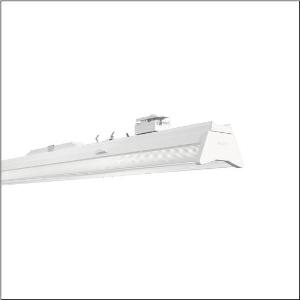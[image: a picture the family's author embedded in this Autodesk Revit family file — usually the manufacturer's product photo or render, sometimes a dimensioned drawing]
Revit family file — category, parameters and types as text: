
# Revit family: licross_r__21_performance_mo_52td16dn4a5g_459a
name_source: partatom
category: Lighting Fixtures
units: mm (PartAtom-declared; Revit-internal decimal feet)

## family parameters
Cut with Voids When Loaded = No
Host = Face
Light Source = No
Part Type = Normal
Room Calculation Point = No
Round Connector Dimension = Use Diameter
Shared = No

## types (1)
- --- (1 x LED, 10840 lm, 62 W, 4000K)
    Apparent Load = 62 VA
    CIE Flux Codes = 66 88 96 79 100
    Color Rendering = 80
    Color Temperature = 4000K
    Default Elevation = 1800 mm
    Description = Licross® 21 Performance MO, luminaire insert, of sheet steel, galvanised, coil coated, white, length: 1.500mm, width: 120mm, height: 123mm, LED rated luminous flux: 10.840lm, light colour: 840, control gear: DALI 2, with plug, 5-pole, with phase selection, mains connection: 220..240V, AC, 50/60Hz, rated input power: 62W, halogen-free wiring, primary light control with lens, of plastic, primary optical cover: cover, of PMMA, light emission: direct/indirect distribution, primary light characteristic: symmetric, protection rating (complete): IP54, insulation class (complete): insulation class I (protective earthing), certification: CE, ENEC, VDE, UKCA, protection symbol: D if used in an environment with non-conductive dust loads with corresponding accessories, impact resistance: IK06, permissible ambient temperature for indoor applications: -25..+35°C, corresponds to IFS (International Featured Standards) requirements for safety and quality in the food industry, reducing of maximum allowable ambient temperature of 5°C with ceiling mounting, LABS conformity tested according to VDMA 24364:2018-05, packaging unit: 1 piece
    Height = 114 mm
    Lamp = 1 x LED
    Lamp Light Flux = 10840 lm
    Lamp Power = 62 W
    Lamp count = 1
    Length = 1500 mm
    Luminous efficacy = 175 lm/W
    Manufacturer = Siteco
    ModVariant = No
    Model = 52TD16DN4A5G
    Mounting Place = Ceiling
    Mounting Type = Pendant
    Number of Poles = 1
    OnlyDefault = Yes
    Power Factor = 1
    Product Name = Licross® 21 Performance MO
    Product group = luminaire insert
    ProductGroupID = 901
    Protection Class = Protection class I
    Protection Degree = IP 54
    RLX_Detail_Level = 1
    RLX_Emergency_Light_Flux = 0 lm
    RLX_Emergency_Type = 0
    RLX_Emergency_Type_DB = No
    RlxData = <blob elided: 34013 chars, md5=18624cc1>
    Socket = socket
    Standby Power = 0 W
    System Light Flux = 10840 lm
    System Power = 62 W
    Type Comments = factory setting: luminous flux: 100 % | dim-lin: 254 | 418 mA
    Type Image = l_1256138.jpg
    URL = http://relux.com
    VarID = @adj_078839
    Voltage = 0 V
    Weight = 0.00 kg
    Width = 120 mm

## geometry (parser evidence)
native form markers: Blend x4, Sweep x11
no freeform markers — native parametric forms only
